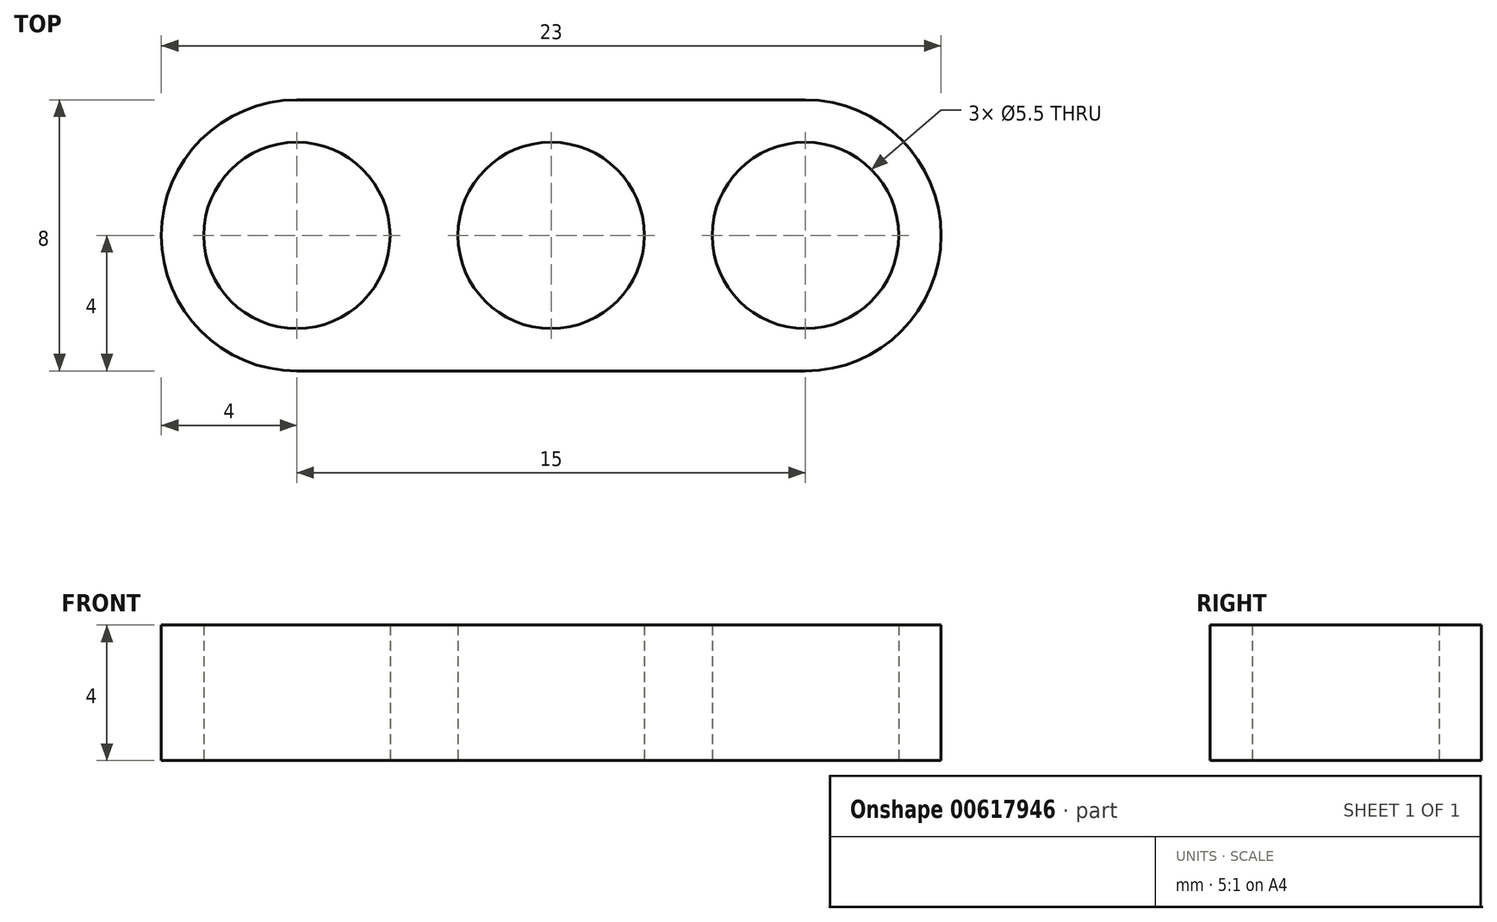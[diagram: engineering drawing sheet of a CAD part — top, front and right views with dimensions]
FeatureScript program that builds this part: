
annotation { "Feature Type Name" : "Feature", "Feature Type Description" : "" }
export const myFeature = defineFeature(function(context is Context, id is Id, definition is map)
    precondition{}
    {
        {
            var Q0;
            Q0=qCreatedBy(makeId("Top.planeOp"),FACE);
            var sketch = newSketch(context, id + "F0", { "sketchPlane" : qUnion([Q0])});
            skCircle(sketch, "E0", {"center": v(0, 0) * mm, "radius": 2.75 * mm});
            skCircle(sketch, "E1.1.0.0", {"center": v(7.5, 0) * mm, "radius": 2.75 * mm});
            skCircle(sketch, "E1.2.0.0", {"center": v(15, 0) * mm, "radius": 2.75 * mm});
            skLineSegment(sketch, "E1.direction1", {"start": v(0, 0) * mm, "end": v(7.5, 0) * mm, "construction": true});
            skLineSegment(sketch, "E2", {"start": v(0, 0) * mm, "end": v(15, 0) * mm, "construction": true});
            skLineSegment(sketch, "E3.bottom", {"start": v(0, -4) * mm, "end": v(15, -4) * mm});
            skLineSegment(sketch, "E3.top", {"start": v(0, 4) * mm, "end": v(15, 4) * mm});
            skArc(sketch, "E4", {"start": v(0, 4) * mm, "mid": v(-4, 0) * mm, "end": v(0, -4) * mm});
            skArc(sketch, "E5", {"start": v(15, -4) * mm, "mid": v(19, 0) * mm, "end": v(15, 4) * mm});
            skLineSegment(sketch, "E6", {"start": v(7.5, 0) * mm, "end": v(7.5, 4) * mm});
            skSolve(sketch);
        }
        {
            var Q0;
            Q0=makeQuery(id+"F0.imprint","IMPRINT",FACE,{"disambiguationData":[TD([[makeQuery(id+"F0.imprint","IMPRINT",EDGE,{"derivedFrom":sQuery(id+"F0.wireOp",EDGE,"E0")}),-1.0]])]});
            extrude(context, id + "F1", {"entities" : qUnion([Q0]), "endBound" : BoundingType.SYMMETRIC, "depth" : 4 * mm, "offsetDistance" : 25 * mm});
        }
    });
